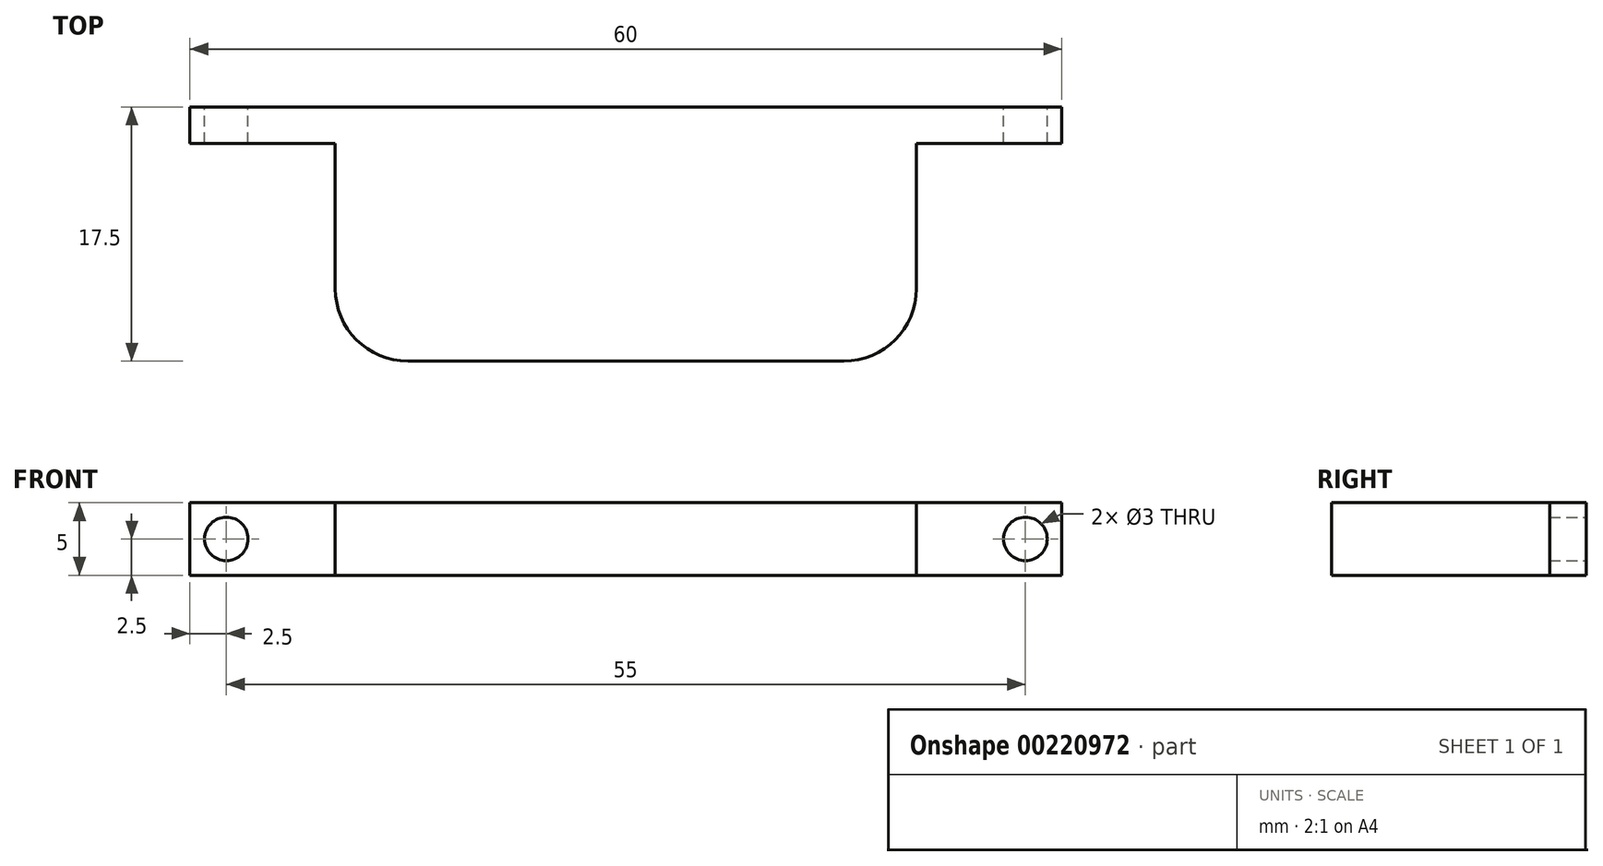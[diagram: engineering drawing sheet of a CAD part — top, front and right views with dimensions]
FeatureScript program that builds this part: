
annotation { "Feature Type Name" : "Feature", "Feature Type Description" : "" }
export const myFeature = defineFeature(function(context is Context, id is Id, definition is map)
    precondition{}
    {
        {
            var Q0;
            Q0=qCreatedBy(makeId("Front.planeOp"),FACE);
            var sketch = newSketch(context, id + "F0", { "sketchPlane" : qUnion([Q0])});
            skLineSegment(sketch, "E0.bottom", {"start": v(0, 0) * mm, "end": v(60, 0) * mm});
            skLineSegment(sketch, "E0.top", {"start": v(0, 5) * mm, "end": v(60, 5) * mm});
            skLineSegment(sketch, "E0.left", {"start": v(0, 0) * mm, "end": v(0, 5) * mm});
            skLineSegment(sketch, "E0.right", {"start": v(60, 0) * mm, "end": v(60, 5) * mm});
            skLineSegment(sketch, "E1", {"start": v(0, 2.5) * mm, "end": v(2.5, 2.5) * mm});
            skLineSegment(sketch, "E2", {"start": v(60, 2.5) * mm, "end": v(57.5, 2.5) * mm});
            skCircle(sketch, "E3", {"center": v(2.5, 2.5) * mm, "radius": 1.5 * mm});
            skCircle(sketch, "E4", {"center": v(57.5, 2.5) * mm, "radius": 1.5 * mm});
            skSolve(sketch);
        }
        {
            var Q0;
            Q0 = qSketchRegion(id + "F0", true);
            extrude(context, id + "F1", {"entities" : qUnion([Q0]), "depth" : 2.5 * mm, "offsetDistance" : 25 * mm});
        }
        {
            var Q0;
            Q0=makeQuery(id+"F1.opExtrude","CAP_FACE",FACE,{"disambiguationData":[OSD([sQuery(id+"F0.wireOp",EDGE,"E0.bottom"),sQuery(id+"F0.wireOp",EDGE,"E0.top"),sQuery(id+"F0.wireOp",EDGE,"E0.left"),sQuery(id+"F0.wireOp",EDGE,"E0.right"),sQuery(id+"F0.wireOp",EDGE,"E3"),sQuery(id+"F0.wireOp",EDGE,"E4")])],"isStart":false});
            var sketch = newSketch(context, id + "F2", { "sketchPlane" : qUnion([Q0])});
            skLineSegment(sketch, "E5", {"start": v(30, 5) * mm, "end": v(10, 5) * mm});
            skLineSegment(sketch, "E6", {"start": v(10, 5) * mm, "end": v(10, 0) * mm});
            skLineSegment(sketch, "E7", {"start": v(10, 0) * mm, "end": v(50, 0) * mm});
            skLineSegment(sketch, "E8", {"start": v(50, 0) * mm, "end": v(50, 5) * mm});
            skLineSegment(sketch, "E9", {"start": v(50, 5) * mm, "end": v(10, 5) * mm});
            skSolve(sketch);
        }
        {
            var Q0;
            Q0 = qSketchRegion(id + "F2", true);
            extrude(context, id + "F3", {"entities" : qUnion([Q0]), "operationType" : NewBodyOperationType.ADD, "depth" : 15 * mm, "offsetDistance" : 25 * mm});
        }
        {
            var Q0;
            Q0=makeQuery(id+"F3.opExtrude","CAP_EDGE",EDGE,{"disambiguationData":[OSD([sQuery(id+"F2.wireOp",EDGE,"E6")])],"isStart":false});
            var Q1;
            Q1=makeQuery(id+"F3.opExtrude","CAP_EDGE",EDGE,{"disambiguationData":[OSD([sQuery(id+"F2.wireOp",EDGE,"E8")])],"isStart":false});
            fillet(context, id + "F4", {"entities" : qUnion([Q0, Q1]), "radius" : 5 * mm, "tangentPropagation" : true, "allowEdgeOverflow" : false});
        }
    });
